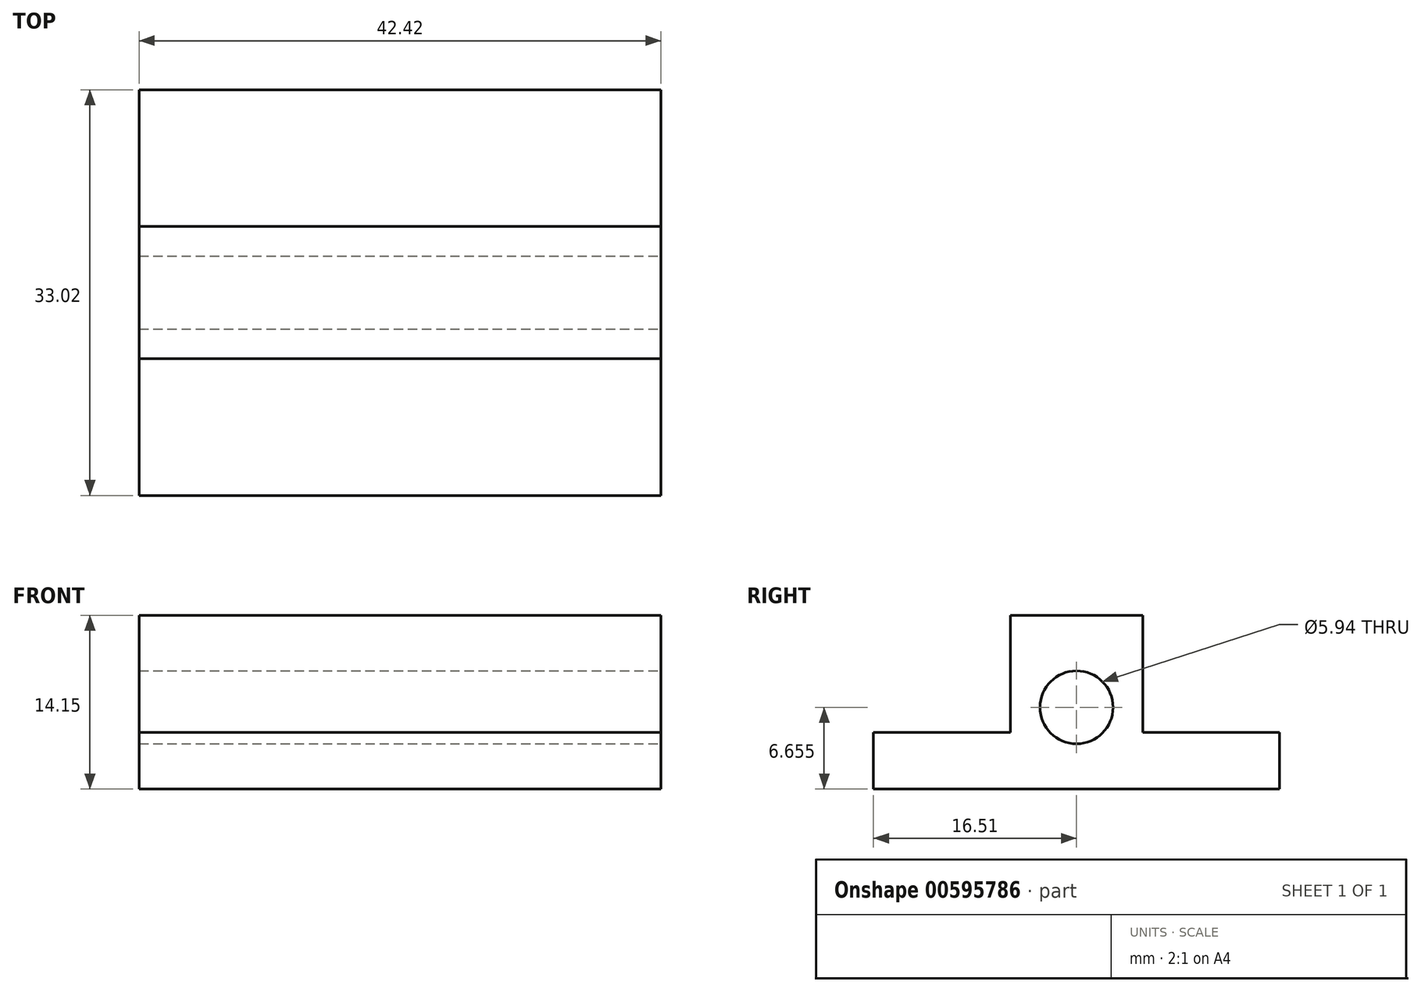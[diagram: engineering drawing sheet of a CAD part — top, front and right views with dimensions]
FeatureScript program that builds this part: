
annotation { "Feature Type Name" : "Feature", "Feature Type Description" : "" }
export const myFeature = defineFeature(function(context is Context, id is Id, definition is map)
    precondition{}
    {
        {
            var Q0;
            Q0=qCreatedBy(makeId("Top.planeOp"),FACE);
            var sketch = newSketch(context, id + "F0", { "sketchPlane" : qUnion([Q0])});
            skLineSegment(sketch, "E0.bottom", {"start": v(21.2, -16.51) * mm, "end": v(-21.2, -16.51) * mm});
            skLineSegment(sketch, "E0.top", {"start": v(21.2, 16.51) * mm, "end": v(-21.2, 16.51) * mm});
            skLineSegment(sketch, "E0.left", {"start": v(21.2, -16.51) * mm, "end": v(21.2, 16.5) * mm});
            skLineSegment(sketch, "E0.right", {"start": v(-21.2, -16.51) * mm, "end": v(-21.2, 16.5) * mm});
            skPoint(sketch, "E0.middle", {"position": v(0, 0) * mm});
            skSolve(sketch);
        }
        {
            var Q0;
            Q0 = qSketchRegion(id + "F0", true);
            extrude(context, id + "F1", {"entities" : qUnion([Q0]), "depth" : 4.62 * mm, "offsetDistance" : 25.4 * mm});
        }
        {
            var Q0;
            Q0=makeQuery(id+"F1.opExtrude","CAP_FACE",FACE,{"disambiguationData":[OSD([sQuery(id+"F0.wireOp",EDGE,"E0.bottom"),sQuery(id+"F0.wireOp",EDGE,"E0.top"),sQuery(id+"F0.wireOp",EDGE,"E0.left"),sQuery(id+"F0.wireOp",EDGE,"E0.right")])],"isStart":false});
            var sketch = newSketch(context, id + "F2", { "sketchPlane" : qUnion([Q0])});
            skLineSegment(sketch, "E1.0", {"start": v(21.2, -5.38) * mm, "end": v(-21.2, -5.38) * mm});
            skLineSegment(sketch, "E2.0", {"start": v(21.2, 5.38) * mm, "end": v(-21.2, 5.38) * mm});
            skLineSegment(sketch, "E3", {"start": v(-21.2, -5.38) * mm, "end": v(-21.2, 5.38) * mm});
            skLineSegment(sketch, "E4", {"start": v(21.2, -5.38) * mm, "end": v(21.2, 5.38) * mm});
            skSolve(sketch);
        }
        {
            var Q0;
            Q0=makeQuery(id+"F2.imprint","IMPRINT",FACE,{"disambiguationData":[TD([[makeQuery(id+"F2.imprint","IMPRINT",EDGE,{"derivedFrom":sQuery(id+"F2.wireOp",EDGE,"E1.0")}),-1.0]])]});
            extrude(context, id + "F3", {"entities" : qUnion([Q0]), "operationType" : NewBodyOperationType.ADD, "depth" : 9.52 * mm, "offsetDistance" : 25.4 * mm});
        }
        {
            var Q0;
            Q0=makeQuery(id+"F3.boolean.opBoolean","MERGE",FACE,{"derivedFrom":[makeQuery(id+"F1.opExtrude","SWEPT_FACE",FACE,{"disambiguationData":[OSD([sQuery(id+"F0.wireOp",EDGE,"E0.left")])]}),makeQuery(id+"F3.opExtrude","SWEPT_FACE",FACE,{"disambiguationData":[OSD([sQuery(id+"F2.wireOp",EDGE,"E4")])]})]});
            var sketch = newSketch(context, id + "F4", { "sketchPlane" : qUnion([Q0])});
            skPoint(sketch, "E5", {"position": v(0, 6.65) * mm});
            skCircle(sketch, "E6", {"center": v(0, 6.65) * mm, "radius": 2.97 * mm});
            skSolve(sketch);
        }
        {
            var Q0;
            Q0=makeQuery(id+"F4.imprint","IMPRINT",FACE,{"disambiguationData":[TD([[makeQuery(id+"F4.imprint","IMPRINT",EDGE,{"derivedFrom":sQuery(id+"F4.wireOp",EDGE,"E6")}),1.0]])]});
            extrude(context, id + "F5", {"entities" : qUnion([Q0]), "operationType" : NewBodyOperationType.REMOVE, "oppositeDirection" : true, "depth" : 50.8 * mm, "offsetDistance" : 25.4 * mm});
        }
    });
